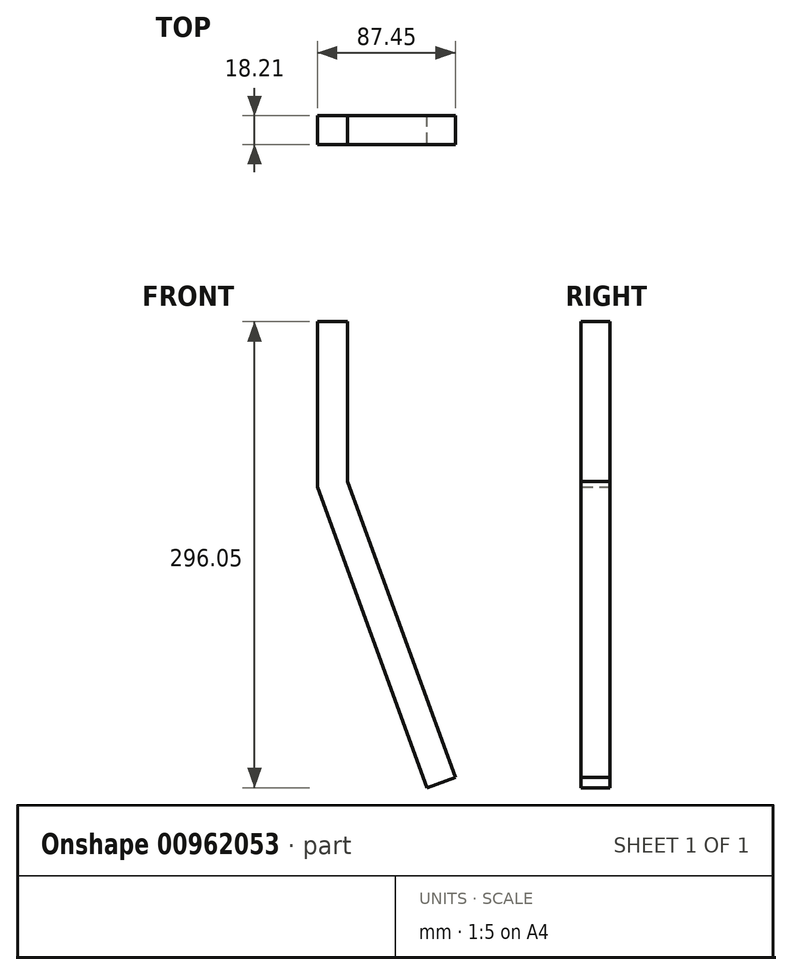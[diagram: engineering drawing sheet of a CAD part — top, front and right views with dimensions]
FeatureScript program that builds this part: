
annotation { "Feature Type Name" : "Feature", "Feature Type Description" : "" }
export const myFeature = defineFeature(function(context is Context, id is Id, definition is map)
    precondition{}
    {
        {
            var Q0;
            Q0=qCreatedBy(makeId("Front.planeOp"),FACE);
            var sketch = newSketch(context, id + "F0", { "sketchPlane" : qUnion([Q0])});
            skLineSegment(sketch, "E0", {"start": v(0, 0) * mm, "end": v(68.4, -187.94) * mm});
            skLineSegment(sketch, "E1", {"start": v(0, 0) * mm, "end": v(0, 101.6) * mm});
            skLineSegment(sketch, "E2", {"start": v(68.4, -187.94) * mm, "end": v(50.5, -194.45) * mm});
            skLineSegment(sketch, "E3", {"start": v(0, 101.6) * mm, "end": v(-19.05, 101.6) * mm});
            skLineSegment(sketch, "E4", {"start": v(-19.05, 101.6) * mm, "end": v(-19.05, -3.36) * mm});
            skLineSegment(sketch, "E5", {"start": v(-19.05, -3.36) * mm, "end": v(50.5, -194.45) * mm});
            skSolve(sketch);
        }
        {
            var Q0;
            Q0 = qSketchRegion(id + "F0", true);
            extrude(context, id + "F1", {"entities" : qUnion([Q0]), "depth" : 18.21 * mm, "offsetDistance" : 25.4 * mm});
        }
    });
